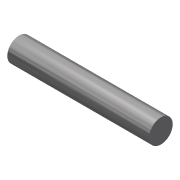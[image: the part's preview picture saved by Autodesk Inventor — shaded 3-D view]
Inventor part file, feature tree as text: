
AUTODESK INVENTOR PART (.ipt)
format: ipt  version: 2016 (Build 200138000, 138)  size: 73,216 bytes
history: native  units: in
note: dims shown in document units (in); Inventor stores cm internally (conversion verified against a paired STEP export)
features: extrude x1, sketch x1
ambient origin geometry x8: Origin, YZ Plane, XZ Plane, XY Plane, X Axis, Y Axis, Z Axis, Center Point
bodies: Solid1 (feature_tree)
feature tree (2):
  extrude  "Extrusion1"  Depth=1.5in TaperAngle=0.0deg
  sketch  "Sketch1"  dims[d0=0.25in d1=1.5in d2=0.0in]
